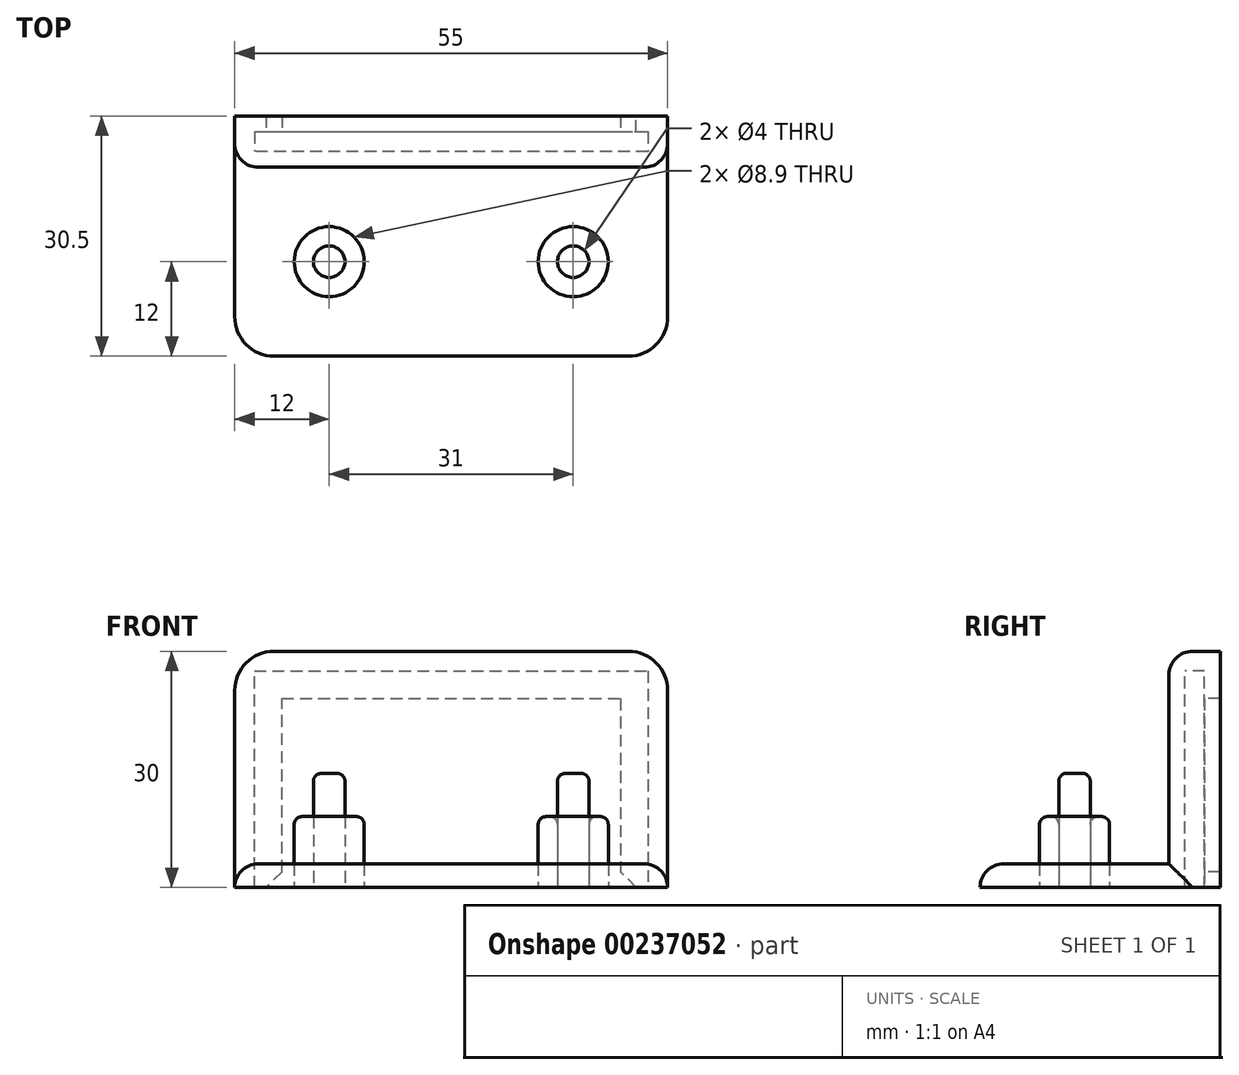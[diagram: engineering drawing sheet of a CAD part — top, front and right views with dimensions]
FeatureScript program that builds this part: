
annotation { "Feature Type Name" : "Feature", "Feature Type Description" : "" }
export const myFeature = defineFeature(function(context is Context, id is Id, definition is map)
    precondition{}
    {
        {
            var Q0;
            Q0=qCreatedBy(makeId("Top.planeOp"),FACE);
            var sketch = newSketch(context, id + "F0", { "sketchPlane" : qUnion([Q0])});
            skLineSegment(sketch, "E0.bottom", {"start": v(27.5, 12) * mm, "end": v(-27.5, 12) * mm});
            skLineSegment(sketch, "E0.top", {"start": v(27.5, -12) * mm, "end": v(-27.5, -12) * mm});
            skLineSegment(sketch, "E0.left", {"start": v(27.5, 12) * mm, "end": v(27.5, -12) * mm});
            skLineSegment(sketch, "E0.right", {"start": v(-27.5, 12) * mm, "end": v(-27.5, -12) * mm});
            skPoint(sketch, "E0.middle", {"position": v(0, 0) * mm});
            skPoint(sketch, "E1", {"position": v(-15.5, 0) * mm});
            skPoint(sketch, "E2", {"position": v(15.5, 0) * mm});
            skCircle(sketch, "E3", {"center": v(-15.5, 0) * mm, "radius": 4.45 * mm});
            skCircle(sketch, "E4", {"center": v(15.5, 0) * mm, "radius": 4.45 * mm});
            skCircle(sketch, "E5", {"center": v(-15.5, 0) * mm, "radius": 2 * mm});
            skCircle(sketch, "E6", {"center": v(15.5, 0) * mm, "radius": 2 * mm});
            skSolve(sketch);
        }
        {
            var Q0;
            Q0=makeQuery(id+"F0.imprint","IMPRINT",FACE,{"disambiguationData":[TD([[makeQuery(id+"F0.imprint","IMPRINT",EDGE,{"derivedFrom":sQuery(id+"F0.wireOp",EDGE,"E5")}),1.0]])]});
            var Q1;
            Q1=makeQuery(id+"F0.imprint","IMPRINT",FACE,{"disambiguationData":[TD([[makeQuery(id+"F0.imprint","IMPRINT",EDGE,{"derivedFrom":sQuery(id+"F0.wireOp",EDGE,"E6")}),1.0]])]});
            extrude(context, id + "F1", {"entities" : qUnion([Q0, Q1]), "depth" : 14.5 * mm});
        }
        {
            var Q0;
            Q0=makeQuery(id+"F0.imprint","IMPRINT",FACE,{"disambiguationData":[TD([[makeQuery(id+"F0.imprint","IMPRINT",EDGE,{"derivedFrom":sQuery(id+"F0.wireOp",EDGE,"E4")}),1.0]])]});
            var Q1;
            Q1=makeQuery(id+"F0.imprint","IMPRINT",FACE,{"disambiguationData":[TD([[makeQuery(id+"F0.imprint","IMPRINT",EDGE,{"derivedFrom":sQuery(id+"F0.wireOp",EDGE,"E3")}),1.0]])]});
            extrude(context, id + "F2", {"entities" : qUnion([Q0, Q1]), "depth" : 9 * mm});
        }
        {
            var Q0;
            Q0=makeQuery(id+"F0.imprint","IMPRINT",FACE,{"disambiguationData":[TD([[makeQuery(id+"F0.imprint","IMPRINT",EDGE,{"derivedFrom":sQuery(id+"F0.wireOp",EDGE,"E0.bottom")}),1.0]])]});
            extrude(context, id + "F3", {"entities" : qUnion([Q0]), "depth" : 3 * mm});
        }
        {
            var Q0;
            Q0=makeQuery(id+"F3.opExtrude","SWEPT_FACE",FACE,{"disambiguationData":[OSD([sQuery(id+"F0.wireOp",EDGE,"E0.bottom")])]});
            var sketch = newSketch(context, id + "F4", { "sketchPlane" : qUnion([Q0])});
            skLineSegment(sketch, "E7.bottom", {"start": v(-27.5, 0) * mm, "end": v(27.5, 0) * mm});
            skLineSegment(sketch, "E7.top", {"start": v(-27.5, 30) * mm, "end": v(27.5, 30) * mm});
            skLineSegment(sketch, "E7.left", {"start": v(-27.5, 0) * mm, "end": v(-27.5, 30) * mm});
            skLineSegment(sketch, "E7.right", {"start": v(27.5, 0) * mm, "end": v(27.5, 30) * mm});
            skSolve(sketch);
        }
        {
            var Q0;
            {var subQ0=sQuery(id+"F4.wireOp",EDGE,"E7.top");Q0=makeQuery(id+"F4.imprint","IMPRINT",FACE,{"disambiguationData":[TD([[makeQuery(id+"F4.imprint","IMPRINT",EDGE,{"derivedFrom":subQ0}),-1.0]])]});}
            var Q1;
            {var subQ0=sQuery(id+"F4.wireOp",EDGE,"E7.bottom");Q1=makeQuery(id+"F4.imprint","IMPRINT",FACE,{"disambiguationData":[TD([[makeQuery(id+"F4.imprint","IMPRINT",EDGE,{"derivedFrom":subQ0}),1.0]])]});}
            extrude(context, id + "F5", {"entities" : qUnion([Q0, Q1]), "operationType" : NewBodyOperationType.ADD, "depth" : 2 * mm});
        }
        {
            var Q0;
            Q0=makeQuery(id+"F5.opExtrude","CAP_FACE",FACE,{"disambiguationData":[OSD([sQuery(id+"F4.wireOp",EDGE,"E7.bottom"),sQuery(id+"F4.wireOp",EDGE,"E7.top"),sQuery(id+"F4.wireOp",EDGE,"E7.left"),sQuery(id+"F4.wireOp",EDGE,"E7.right")])],"isStart":false});
            var sketch = newSketch(context, id + "F6", { "sketchPlane" : qUnion([Q0])});
            skLineSegment(sketch, "E8", {"start": v(-27.5, 0) * mm, "end": v(-27.5, 30) * mm});
            skLineSegment(sketch, "E9", {"start": v(-27.5, 30) * mm, "end": v(27.5, 30) * mm});
            skLineSegment(sketch, "E10", {"start": v(27.5, 30) * mm, "end": v(27.5, 0) * mm});
            skLineSegment(sketch, "E11", {"start": v(27.5, 0) * mm, "end": v(25, 0) * mm});
            skLineSegment(sketch, "E12", {"start": v(25, 0) * mm, "end": v(25, 27.5) * mm});
            skLineSegment(sketch, "E13", {"start": v(25, 27.5) * mm, "end": v(-25, 27.5) * mm});
            skLineSegment(sketch, "E14", {"start": v(-25, 27.5) * mm, "end": v(-25, 0) * mm});
            skLineSegment(sketch, "E15", {"start": v(-25, 0) * mm, "end": v(-27.5, 0) * mm});
            skSolve(sketch);
        }
        {
            var Q0;
            Q0=makeQuery(id+"F6.imprint","IMPRINT",FACE,{"disambiguationData":[TD([[makeQuery(id+"F6.imprint","IMPRINT",EDGE,{"derivedFrom":sQuery(id+"F6.wireOp",EDGE,"E8")}),-1.0]])]});
            extrude(context, id + "F7", {"entities" : qUnion([Q0]), "operationType" : NewBodyOperationType.ADD, "depth" : 2.5 * mm});
        }
        {
            var Q0;
            Q0=makeQuery(id+"F7.opExtrude","CAP_FACE",FACE,{"disambiguationData":[OSD([sQuery(id+"F6.wireOp",EDGE,"E8"),sQuery(id+"F6.wireOp",EDGE,"E9"),sQuery(id+"F6.wireOp",EDGE,"E10"),sQuery(id+"F6.wireOp",EDGE,"E11"),sQuery(id+"F6.wireOp",EDGE,"E12"),sQuery(id+"F6.wireOp",EDGE,"E13"),sQuery(id+"F6.wireOp",EDGE,"E14"),sQuery(id+"F6.wireOp",EDGE,"E15")])],"isStart":false});
            var sketch = newSketch(context, id + "F8", { "sketchPlane" : qUnion([Q0])});
            skLineSegment(sketch, "E16", {"start": v(-27.5, 0) * mm, "end": v(-27.5, 30) * mm});
            skLineSegment(sketch, "E17", {"start": v(-27.5, 30) * mm, "end": v(27.5, 30) * mm});
            skLineSegment(sketch, "E18", {"start": v(27.5, 30) * mm, "end": v(27.5, 0) * mm});
            skLineSegment(sketch, "E19", {"start": v(27.5, 0) * mm, "end": v(21.5, 0) * mm});
            skLineSegment(sketch, "E20", {"start": v(21.5, 0) * mm, "end": v(21.5, 24) * mm});
            skLineSegment(sketch, "E21", {"start": v(21.5, 24) * mm, "end": v(-21.5, 24) * mm});
            skLineSegment(sketch, "E22", {"start": v(-21.5, 24) * mm, "end": v(-21.5, 0) * mm});
            skLineSegment(sketch, "E23", {"start": v(-21.5, 0) * mm, "end": v(-27.5, 0) * mm});
            skSolve(sketch);
        }
        {
            var Q0;
            {var subQ2=sQuery(id+"F8.wireOp",EDGE,"E20");Q0=makeQuery(id+"F8.imprint","IMPRINT",FACE,{"disambiguationData":[TD([[makeQuery(id+"F8.imprint","IMPRINT",EDGE,{"derivedFrom":subQ2}),-1.0]])]});}
            var Q1;
            {var subQ3=sQuery(id+"F8.wireOp",EDGE,"E16");Q1=makeQuery(id+"F8.imprint","IMPRINT",FACE,{"disambiguationData":[TD([[makeQuery(id+"F8.imprint","IMPRINT",EDGE,{"derivedFrom":subQ3}),-1.0]])]});}
            extrude(context, id + "F9", {"entities" : qUnion([Q0, Q1]), "operationType" : NewBodyOperationType.ADD, "depth" : 2 * mm});
        }
        {
            var Q0;
            Q0=makeQuery(id+"F9.boolean.opBoolean","MERGE",EDGE,{"derivedFrom":[makeQuery(id+"F7.boolean.opBoolean","MERGE",EDGE,{"derivedFrom":[makeQuery(id+"F5.opExtrude","SWEPT_EDGE",EDGE,{"disambiguationData":[OSD([sQuery(id+"F4.wireOp",EDGE,"E7.top"),sQuery(id+"F4.wireOp",EDGE,"E7.left")])]}),makeQuery(id+"F7.opExtrude","SWEPT_EDGE",EDGE,{"disambiguationData":[OSD([sQuery(id+"F6.wireOp",EDGE,"E8"),sQuery(id+"F6.wireOp",EDGE,"E9")])]})]}),makeQuery(id+"F9.opExtrude","SWEPT_EDGE",EDGE,{"disambiguationData":[OSD([sQuery(id+"F8.wireOp",EDGE,"E16"),sQuery(id+"F8.wireOp",EDGE,"E17")])]})]});
            var Q1;
            Q1=makeQuery(id+"F9.boolean.opBoolean","MERGE",EDGE,{"derivedFrom":[makeQuery(id+"F7.boolean.opBoolean","MERGE",EDGE,{"derivedFrom":[makeQuery(id+"F5.opExtrude","SWEPT_EDGE",EDGE,{"disambiguationData":[OSD([sQuery(id+"F4.wireOp",EDGE,"E7.top"),sQuery(id+"F4.wireOp",EDGE,"E7.right")])]}),makeQuery(id+"F7.opExtrude","SWEPT_EDGE",EDGE,{"disambiguationData":[OSD([sQuery(id+"F6.wireOp",EDGE,"E9"),sQuery(id+"F6.wireOp",EDGE,"E10")])]})]}),makeQuery(id+"F9.opExtrude","SWEPT_EDGE",EDGE,{"disambiguationData":[OSD([sQuery(id+"F8.wireOp",EDGE,"E17"),sQuery(id+"F8.wireOp",EDGE,"E18")])]})]});
            var Q2;
            Q2=makeQuery(id+"F3.opExtrude","SWEPT_EDGE",EDGE,{"disambiguationData":[OSD([sQuery(id+"F0.wireOp",EDGE,"E0.top"),sQuery(id+"F0.wireOp",EDGE,"E0.right")])]});
            var Q3;
            Q3=makeQuery(id+"F3.opExtrude","SWEPT_EDGE",EDGE,{"disambiguationData":[OSD([sQuery(id+"F0.wireOp",EDGE,"E0.top"),sQuery(id+"F0.wireOp",EDGE,"E0.left")])]});
            fillet(context, id + "F10", {"entities" : qUnion([Q0, Q1, Q2, Q3]), "radius" : 5 * mm, "tangentPropagation" : true, "allowEdgeOverflow" : false});
        }
        {
            var Q0;
            Q0=makeQuery(id+"F3.opExtrude","CAP_EDGE",EDGE,{"disambiguationData":[OSD([sQuery(id+"F0.wireOp",EDGE,"E0.top")])],"isStart":false});
            var Q1;
            Q1=makeQuery(id+"F5.opExtrude","CAP_EDGE",EDGE,{"disambiguationData":[OSD([sQuery(id+"F4.wireOp",EDGE,"E7.top")])],"isStart":true});
            fillet(context, id + "F11", {"entities" : qUnion([Q0, Q1]), "radius" : 3 * mm, "tangentPropagation" : true, "allowEdgeOverflow" : false});
        }
        {
            var Q0;
            Q0=makeQuery(id+"F1.opExtrude","CAP_EDGE",EDGE,{"disambiguationData":[OSD([sQuery(id+"F0.wireOp",EDGE,"E5")])],"isStart":false});
            var Q1;
            Q1=makeQuery(id+"F2.opExtrude","CAP_EDGE",EDGE,{"disambiguationData":[OSD([sQuery(id+"F0.wireOp",EDGE,"E3")])],"isStart":false});
            var Q2;
            Q2=makeQuery(id+"F1.opExtrude","CAP_EDGE",EDGE,{"disambiguationData":[OSD([sQuery(id+"F0.wireOp",EDGE,"E6")])],"isStart":false});
            var Q3;
            Q3=makeQuery(id+"F2.opExtrude","CAP_FACE",FACE,{"disambiguationData":[OSD([sQuery(id+"F0.wireOp",EDGE,"E4"),sQuery(id+"F0.wireOp",EDGE,"E6")])],"isStart":false});
            fillet(context, id + "F12", {"entities" : qUnion([Q0, Q1, Q2, Q3]), "radius" : 1 * mm, "tangentPropagation" : true, "allowEdgeOverflow" : false});
        }
        {
            var Q0;
            Q0=makeQuery(id+"F9.opExtrude","SWEPT_EDGE",EDGE,{"disambiguationData":[OSD([sQuery(id+"F8.wireOp",EDGE,"E19"),sQuery(id+"F8.wireOp",EDGE,"E20")])]});
            var Q1;
            Q1=makeQuery(id+"F9.opExtrude","SWEPT_EDGE",EDGE,{"disambiguationData":[OSD([sQuery(id+"F8.wireOp",EDGE,"E22"),sQuery(id+"F8.wireOp",EDGE,"E23")])]});
            chamfer(context, id + "F13", {"entities" : qUnion([Q0, Q1]), "width" : 2 * mm, "tangentPropagation" : true});
        }
    });
